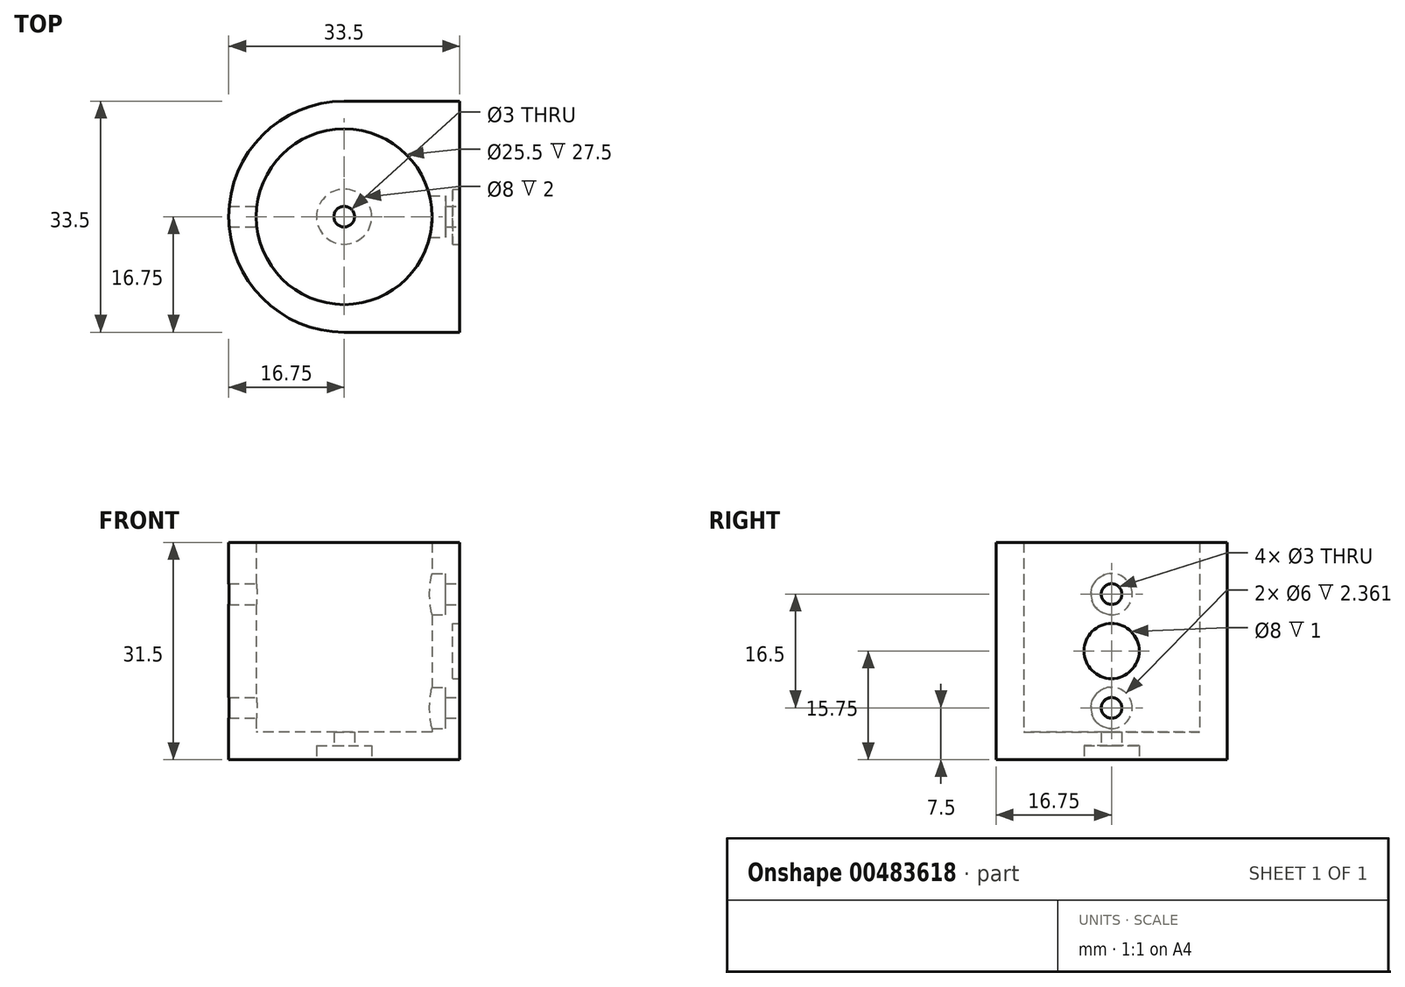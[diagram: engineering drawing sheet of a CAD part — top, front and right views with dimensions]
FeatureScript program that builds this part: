
annotation { "Feature Type Name" : "Feature", "Feature Type Description" : "" }
export const myFeature = defineFeature(function(context is Context, id is Id, definition is map)
    precondition{}
    {
        {
            var Q0;
            Q0=qCreatedBy(makeId("Top.planeOp"),FACE);
            var sketch = newSketch(context, id + "F0", { "sketchPlane" : qUnion([Q0])});
            skCircle(sketch, "E0", {"center": v(0, 0) * mm, "radius": 14.75 * mm});
            skLineSegment(sketch, "E1.bottom", {"start": v(14.75, 14.75) * mm, "end": v(-14.75, 14.75) * mm});
            skLineSegment(sketch, "E1.top", {"start": v(14.75, -14.75) * mm, "end": v(-14.75, -14.75) * mm});
            skLineSegment(sketch, "E1.left", {"start": v(14.75, 14.75) * mm, "end": v(14.75, -14.75) * mm});
            skLineSegment(sketch, "E1.right", {"start": v(-14.75, 14.75) * mm, "end": v(-14.75, -14.75) * mm});
            skLineSegment(sketch, "E2.bottom", {"start": v(16.75, 16.75) * mm, "end": v(-16.75, 16.75) * mm});
            skLineSegment(sketch, "E2.top", {"start": v(16.75, -16.75) * mm, "end": v(-16.75, -16.75) * mm});
            skLineSegment(sketch, "E2.left", {"start": v(16.75, 16.75) * mm, "end": v(16.75, -16.75) * mm});
            skLineSegment(sketch, "E2.right", {"start": v(-16.75, 16.75) * mm, "end": v(-16.75, -16.75) * mm});
            skLineSegment(sketch, "E3", {"start": v(0, 16.75) * mm, "end": v(0, -16.75) * mm});
            skCircle(sketch, "E4", {"center": v(0, 0) * mm, "radius": 12.75 * mm});
            skCircle(sketch, "E5", {"center": v(0, 0) * mm, "radius": 16.75 * mm});
            skSolve(sketch);
        }
        {
            var Q0;
            {var subQ0=sQuery(id+"F0.wireOp",EDGE,"E5");var subQ1=sQuery(id+"F0.wireOp",EDGE,"E1.top");var subQ2=makeQuery(id+"F0.imprint","INTERSECT",VERTEX,{"disambiguationData":[OD(0.0)],"derivedFrom":[subQ1,subQ0]});Q0=makeQuery(id+"F0.imprint","IMPRINT",FACE,{"disambiguationData":[TD([[makeQuery(id+"F0.imprint","IMPRINT",EDGE,{"disambiguationData":[TD([[subQ2,-1.0]])],"derivedFrom":subQ1}),1.0]])]});}
            var Q1;
            {var subQ5=sQuery(id+"F0.wireOp",EDGE,"E1.top");var subQ8=sQuery(id+"F0.wireOp",EDGE,"E1.left");var subQ9=makeQuery(id+"F0.imprint","INTERSECT",VERTEX,{"derivedFrom":[subQ5,subQ8]});Q1=makeQuery(id+"F0.imprint","IMPRINT",FACE,{"disambiguationData":[TD([[makeQuery(id+"F0.imprint","IMPRINT",EDGE,{"disambiguationData":[TD([[subQ9,-1.0]])],"derivedFrom":subQ5}),1.0]])]});}
            var Q2;
            {var subQ0=sQuery(id+"F0.wireOp",EDGE,"E1.left");var subQ1=sQuery(id+"F0.wireOp",EDGE,"E1.top");var subQ2=makeQuery(id+"F0.imprint","INTERSECT",VERTEX,{"derivedFrom":[subQ1,subQ0]});Q2=makeQuery(id+"F0.imprint","IMPRINT",FACE,{"disambiguationData":[TD([[makeQuery(id+"F0.imprint","IMPRINT",EDGE,{"disambiguationData":[TD([[subQ2,-1.0]])],"derivedFrom":subQ1}),-1.0]])]});}
            var Q3;
            {var subQ0=sQuery(id+"F0.wireOp",EDGE,"E1.left");var subQ1=sQuery(id+"F0.wireOp",EDGE,"E0");var subQ2=makeQuery(id+"F0.imprint","INTERSECT",VERTEX,{"derivedFrom":[subQ1,subQ0]});Q3=makeQuery(id+"F0.imprint","IMPRINT",FACE,{"disambiguationData":[TD([[makeQuery(id+"F0.imprint","IMPRINT",EDGE,{"disambiguationData":[TD([[subQ2,-1.0]])],"derivedFrom":subQ0}),-1.0]])]});}
            var Q4;
            {var subQ0=sQuery(id+"F0.wireOp",EDGE,"E4");var subQ1=sQuery(id+"F0.wireOp",EDGE,"E3");var subQ5=makeQuery(id+"F0.imprint","INTERSECT",VERTEX,{"disambiguationData":[OD(0.0)],"derivedFrom":[subQ1,subQ0]});Q4=makeQuery(id+"F0.imprint","IMPRINT",FACE,{"disambiguationData":[TD([[makeQuery(id+"F0.imprint","IMPRINT",EDGE,{"disambiguationData":[TD([[subQ5,1.0]])],"derivedFrom":subQ0}),-1.0]])]});}
            var Q5;
            {var subQ0=sQuery(id+"F0.wireOp",EDGE,"E1.left");var subQ1=makeQuery(id+"F0.imprint","INTERSECT",VERTEX,{"derivedFrom":[sQuery(id+"F0.wireOp",EDGE,"E0"),subQ0]});Q5=makeQuery(id+"F0.imprint","IMPRINT",FACE,{"disambiguationData":[TD([[makeQuery(id+"F0.imprint","IMPRINT",EDGE,{"disambiguationData":[TD([[subQ1,1.0]])],"derivedFrom":subQ0}),1.0]])]});}
            var Q6;
            {var subQ0=sQuery(id+"F0.wireOp",EDGE,"E1.left");var subQ1=sQuery(id+"F0.wireOp",EDGE,"E0");var subQ2=makeQuery(id+"F0.imprint","INTERSECT",VERTEX,{"derivedFrom":[subQ1,subQ0]});Q6=makeQuery(id+"F0.imprint","IMPRINT",FACE,{"disambiguationData":[TD([[makeQuery(id+"F0.imprint","IMPRINT",EDGE,{"disambiguationData":[TD([[subQ2,1.0]])],"derivedFrom":subQ0}),-1.0]])]});}
            var Q7;
            {var subQ5=sQuery(id+"F0.wireOp",EDGE,"E1.left");var subQ6=sQuery(id+"F0.wireOp",EDGE,"E1.bottom");var subQ7=makeQuery(id+"F0.imprint","INTERSECT",VERTEX,{"derivedFrom":[subQ6,subQ5]});Q7=makeQuery(id+"F0.imprint","IMPRINT",FACE,{"disambiguationData":[TD([[makeQuery(id+"F0.imprint","IMPRINT",EDGE,{"disambiguationData":[TD([[subQ7,-1.0]])],"derivedFrom":subQ6}),-1.0]])]});}
            var Q8;
            {var subQ0=sQuery(id+"F0.wireOp",EDGE,"E1.left");var subQ1=sQuery(id+"F0.wireOp",EDGE,"E1.bottom");var subQ2=makeQuery(id+"F0.imprint","INTERSECT",VERTEX,{"derivedFrom":[subQ1,subQ0]});Q8=makeQuery(id+"F0.imprint","IMPRINT",FACE,{"disambiguationData":[TD([[makeQuery(id+"F0.imprint","IMPRINT",EDGE,{"disambiguationData":[TD([[subQ2,-1.0]])],"derivedFrom":subQ1}),1.0]])]});}
            var Q9;
            {var subQ0=sQuery(id+"F0.wireOp",EDGE,"E5");var subQ1=sQuery(id+"F0.wireOp",EDGE,"E1.bottom");var subQ2=makeQuery(id+"F0.imprint","INTERSECT",VERTEX,{"disambiguationData":[OD(0.0)],"derivedFrom":[subQ1,subQ0]});Q9=makeQuery(id+"F0.imprint","IMPRINT",FACE,{"disambiguationData":[TD([[makeQuery(id+"F0.imprint","IMPRINT",EDGE,{"disambiguationData":[TD([[subQ2,-1.0]])],"derivedFrom":subQ1}),-1.0]])]});}
            var Q10;
            {var subQ0=sQuery(id+"F0.wireOp",EDGE,"E4");var subQ1=sQuery(id+"F0.wireOp",EDGE,"E3");var subQ2=makeQuery(id+"F0.imprint","INTERSECT",VERTEX,{"disambiguationData":[OD(0.0)],"derivedFrom":[subQ1,subQ0]});Q10=makeQuery(id+"F0.imprint","IMPRINT",FACE,{"disambiguationData":[TD([[makeQuery(id+"F0.imprint","IMPRINT",EDGE,{"disambiguationData":[TD([[subQ2,-1.0]])],"derivedFrom":subQ0}),-1.0]])]});}
            var Q11;
            {var subQ0=sQuery(id+"F0.wireOp",EDGE,"E1.right");var subQ1=sQuery(id+"F0.wireOp",EDGE,"E0");var subQ2=makeQuery(id+"F0.imprint","INTERSECT",VERTEX,{"derivedFrom":[subQ1,subQ0]});Q11=makeQuery(id+"F0.imprint","IMPRINT",FACE,{"disambiguationData":[TD([[makeQuery(id+"F0.imprint","IMPRINT",EDGE,{"disambiguationData":[TD([[subQ2,1.0]])],"derivedFrom":subQ0}),1.0]])]});}
            var Q12;
            {var subQ0=sQuery(id+"F0.wireOp",EDGE,"E5");var subQ1=sQuery(id+"F0.wireOp",EDGE,"E1.bottom");var subQ2=makeQuery(id+"F0.imprint","INTERSECT",VERTEX,{"disambiguationData":[OD(1.0)],"derivedFrom":[subQ1,subQ0]});Q12=makeQuery(id+"F0.imprint","IMPRINT",FACE,{"disambiguationData":[TD([[makeQuery(id+"F0.imprint","IMPRINT",EDGE,{"disambiguationData":[TD([[subQ2,1.0]])],"derivedFrom":subQ1}),-1.0]])]});}
            var Q13;
            {var subQ0=sQuery(id+"F0.wireOp",EDGE,"E1.right");var subQ1=makeQuery(id+"F0.imprint","INTERSECT",VERTEX,{"derivedFrom":[sQuery(id+"F0.wireOp",EDGE,"E0"),subQ0]});Q13=makeQuery(id+"F0.imprint","IMPRINT",FACE,{"disambiguationData":[TD([[makeQuery(id+"F0.imprint","IMPRINT",EDGE,{"disambiguationData":[TD([[subQ1,1.0]])],"derivedFrom":subQ0}),-1.0]])]});}
            var Q14;
            {var subQ0=sQuery(id+"F0.wireOp",EDGE,"E1.right");var subQ1=sQuery(id+"F0.wireOp",EDGE,"E0");var subQ2=makeQuery(id+"F0.imprint","INTERSECT",VERTEX,{"derivedFrom":[subQ1,subQ0]});Q14=makeQuery(id+"F0.imprint","IMPRINT",FACE,{"disambiguationData":[TD([[makeQuery(id+"F0.imprint","IMPRINT",EDGE,{"disambiguationData":[TD([[subQ2,-1.0]])],"derivedFrom":subQ0}),1.0]])]});}
            var Q15;
            {var subQ0=sQuery(id+"F0.wireOp",EDGE,"E5");var subQ1=sQuery(id+"F0.wireOp",EDGE,"E1.top");var subQ2=makeQuery(id+"F0.imprint","INTERSECT",VERTEX,{"disambiguationData":[OD(1.0)],"derivedFrom":[subQ1,subQ0]});Q15=makeQuery(id+"F0.imprint","IMPRINT",FACE,{"disambiguationData":[TD([[makeQuery(id+"F0.imprint","IMPRINT",EDGE,{"disambiguationData":[TD([[subQ2,1.0]])],"derivedFrom":subQ1}),1.0]])]});}
            extrude(context, id + "F1", {"entities" : qUnion([Q0, Q1, Q2, Q3, Q4, Q5, Q6, Q7, Q8, Q9, Q10, Q11, Q12, Q13, Q14, Q15]), "depth" : 31.5 * mm});
        }
        {
            var Q0;
            Q0=makeQuery(id+"F1.opExtrude","SWEPT_FACE",FACE,{"disambiguationData":[OSD([sQuery(id+"F0.wireOp",EDGE,"E2.left")])]});
            var sketch = newSketch(context, id + "F2", { "sketchPlane" : qUnion([Q0])});
            skPoint(sketch, "E6", {"position": v(0, 15.75) * mm});
            skPoint(sketch, "E6.positionSnap0", {"position": v(16.75, 15.75) * mm});
            skCircle(sketch, "E7", {"center": v(0, 15.75) * mm, "radius": 12.75 * mm});
            skPoint(sketch, "E8", {"position": v(0, 24) * mm});
            skCircle(sketch, "E9", {"center": v(0, 24) * mm, "radius": 1.5 * mm});
            skPoint(sketch, "E10.1.0", {"position": v(0, 7.5) * mm});
            skCircle(sketch, "E10.1.1", {"center": v(0, 7.5) * mm, "radius": 1.5 * mm});
            skCircle(sketch, "E11", {"center": v(0, 24) * mm, "radius": 3 * mm});
            skCircle(sketch, "E12.1.0", {"center": v(0, 7.5) * mm, "radius": 3 * mm});
            skCircle(sketch, "E13", {"center": v(0, 15.75) * mm, "radius": 4 * mm});
            skSolve(sketch);
        }
        {
            var Q0;
            Q0=makeQuery(id+"F2.imprint","IMPRINT",FACE,{"disambiguationData":[TD([[makeQuery(id+"F2.imprint","IMPRINT",EDGE,{"derivedFrom":sQuery(id+"F2.wireOp",EDGE,"E9")}),1.0]])]});
            var Q1;
            Q1=makeQuery(id+"F2.imprint","IMPRINT",FACE,{"disambiguationData":[TD([[makeQuery(id+"F2.imprint","IMPRINT",EDGE,{"derivedFrom":sQuery(id+"F2.wireOp",EDGE,"E10.1.1")}),1.0]])]});
            var Q2;
            Q2=makeQuery(id+"F2.imprint","IMPRINT",FACE,{"disambiguationData":[TD([[makeQuery(id+"F2.imprint","IMPRINT",EDGE,{"derivedFrom":sQuery(id+"F2.wireOp",EDGE,"E9")}),-1.0]])]});
            var Q3;
            Q3=makeQuery(id+"F2.imprint","IMPRINT",FACE,{"disambiguationData":[TD([[makeQuery(id+"F2.imprint","IMPRINT",EDGE,{"derivedFrom":sQuery(id+"F2.wireOp",EDGE,"E10.1.1")}),-1.0]])]});
            extrude(context, id + "F3", {"entities" : qUnion([Q0, Q1, Q2, Q3]), "operationType" : NewBodyOperationType.REMOVE, "oppositeDirection" : true, "depth" : 5 * mm});
        }
        {
            var Q0;
            Q0=makeQuery(id+"F2.imprint","IMPRINT",FACE,{"disambiguationData":[TD([[makeQuery(id+"F2.imprint","IMPRINT",EDGE,{"derivedFrom":sQuery(id+"F2.wireOp",EDGE,"E9")}),-1.0]])]});
            var Q1;
            Q1=makeQuery(id+"F2.imprint","IMPRINT",FACE,{"disambiguationData":[TD([[makeQuery(id+"F2.imprint","IMPRINT",EDGE,{"derivedFrom":sQuery(id+"F2.wireOp",EDGE,"E10.1.1")}),-1.0]])]});
            extrude(context, id + "F4", {"entities" : qUnion([Q0, Q1]), "operationType" : NewBodyOperationType.ADD, "oppositeDirection" : true, "depth" : 2 * mm});
        }
        {
            var Q0;
            Q0=makeQuery(id+"F2.imprint","IMPRINT",FACE,{"disambiguationData":[TD([[makeQuery(id+"F2.imprint","IMPRINT",EDGE,{"derivedFrom":sQuery(id+"F2.wireOp",EDGE,"E13")}),1.0]])]});
            extrude(context, id + "F5", {"entities" : qUnion([Q0]), "operationType" : NewBodyOperationType.REMOVE, "oppositeDirection" : true, "depth" : 1 * mm});
        }
        {
            var Q0;
            {var subQ0=sQuery(id+"F0.wireOp",EDGE,"E4");var subQ1=sQuery(id+"F0.wireOp",EDGE,"E3");var subQ2=makeQuery(id+"F0.imprint","INTERSECT",VERTEX,{"disambiguationData":[OD(0.0)],"derivedFrom":[subQ1,subQ0]});Q0=makeQuery(id+"F0.imprint","IMPRINT",FACE,{"disambiguationData":[TD([[makeQuery(id+"F0.imprint","IMPRINT",EDGE,{"disambiguationData":[TD([[subQ2,-1.0]])],"derivedFrom":subQ1}),1.0]])]});}
            var Q1;
            {var subQ0=sQuery(id+"F0.wireOp",EDGE,"E4");var subQ1=sQuery(id+"F0.wireOp",EDGE,"E3");var subQ2=makeQuery(id+"F0.imprint","INTERSECT",VERTEX,{"disambiguationData":[OD(0.0)],"derivedFrom":[subQ1,subQ0]});Q1=makeQuery(id+"F0.imprint","IMPRINT",FACE,{"disambiguationData":[TD([[makeQuery(id+"F0.imprint","IMPRINT",EDGE,{"disambiguationData":[TD([[subQ2,-1.0]])],"derivedFrom":subQ1}),-1.0]])]});}
            extrude(context, id + "F6", {"entities" : qUnion([Q0, Q1]), "operationType" : NewBodyOperationType.ADD, "depth" : 4 * mm});
        }
        {
            var Q0;
            {var subQ0=sQuery(id+"F0.wireOp",EDGE,"E4");Q0=makeQuery(id+"F6.boolean.opBoolean","MERGE",FACE,{"derivedFrom":[makeQuery(id+"F1.opExtrude","CAP_FACE",FACE,{"disambiguationData":[OSD([sQuery(id+"F0.wireOp",EDGE,"E2.bottom"),sQuery(id+"F0.wireOp",EDGE,"E2.top"),sQuery(id+"F0.wireOp",EDGE,"E2.left"),subQ0,sQuery(id+"F0.wireOp",EDGE,"E5")])],"isStart":true}),makeQuery(id+"F6.opExtrude","CAP_FACE",FACE,{"disambiguationData":[OSD([subQ0])],"isStart":true})]});}
            var sketch = newSketch(context, id + "F7", { "sketchPlane" : qUnion([Q0])});
            skCircle(sketch, "E14", {"center": v(0, 0) * mm, "radius": 1.5 * mm});
            skCircle(sketch, "E15", {"center": v(0, 0) * mm, "radius": 4 * mm});
            skSolve(sketch);
        }
        {
            var Q0;
            Q0=makeQuery(id+"F7.imprint","IMPRINT",FACE,{"disambiguationData":[TD([[makeQuery(id+"F7.imprint","IMPRINT",EDGE,{"derivedFrom":sQuery(id+"F7.wireOp",EDGE,"E14")}),1.0]])]});
            extrude(context, id + "F8", {"entities" : qUnion([Q0]), "operationType" : NewBodyOperationType.REMOVE, "endBound" : BoundingType.THROUGH_ALL, "oppositeDirection" : true, "depth" : 25 * mm});
        }
        {
            var Q0;
            Q0=makeQuery(id+"F7.imprint","IMPRINT",FACE,{"disambiguationData":[TD([[makeQuery(id+"F7.imprint","IMPRINT",EDGE,{"derivedFrom":sQuery(id+"F7.wireOp",EDGE,"E14")}),-1.0]])]});
            extrude(context, id + "F9", {"entities" : qUnion([Q0]), "operationType" : NewBodyOperationType.REMOVE, "oppositeDirection" : true, "depth" : 2 * mm});
        }
        {
            var Q0;
            Q0=makeQuery(id+"F2.imprint","IMPRINT",FACE,{"disambiguationData":[TD([[makeQuery(id+"F2.imprint","IMPRINT",EDGE,{"derivedFrom":sQuery(id+"F2.wireOp",EDGE,"E9")}),1.0]])]});
            var Q1;
            Q1=makeQuery(id+"F2.imprint","IMPRINT",FACE,{"disambiguationData":[TD([[makeQuery(id+"F2.imprint","IMPRINT",EDGE,{"derivedFrom":sQuery(id+"F2.wireOp",EDGE,"E10.1.1")}),1.0]])]});
            extrude(context, id + "F10", {"entities" : qUnion([Q0, Q1]), "operationType" : NewBodyOperationType.REMOVE, "endBound" : BoundingType.THROUGH_ALL, "oppositeDirection" : true, "depth" : 25 * mm});
        }
    });
